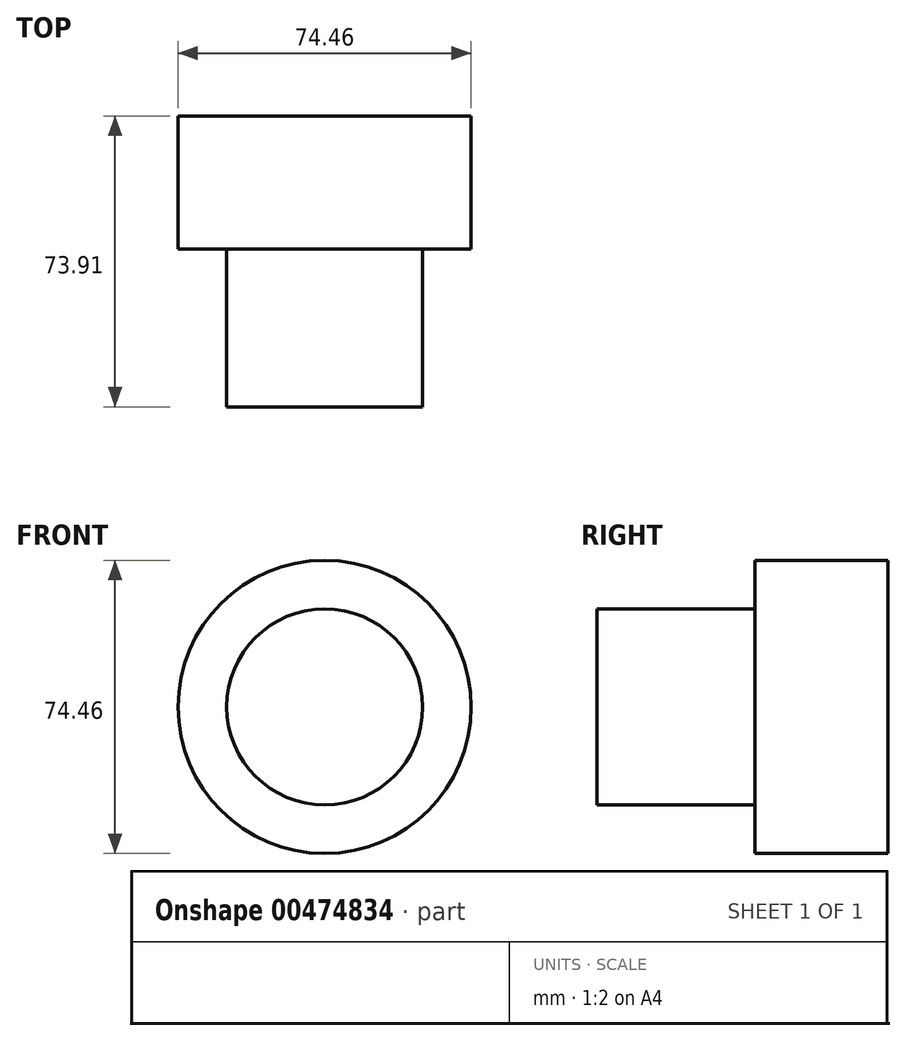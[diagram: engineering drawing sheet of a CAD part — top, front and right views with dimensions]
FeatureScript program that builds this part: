
annotation { "Feature Type Name" : "Feature", "Feature Type Description" : "" }
export const myFeature = defineFeature(function(context is Context, id is Id, definition is map)
    precondition{}
    {
        {
            var Q0;
            Q0=qCreatedBy(makeId("Front.planeOp"),FACE);
            var sketch = newSketch(context, id + "F0", { "sketchPlane" : qUnion([Q0])});
            skCircle(sketch, "E0", {"center": v(0, 0) * mm, "radius": 37.23 * mm});
            skSolve(sketch);
        }
        {
            var Q0;
            Q0=makeQuery(id+"F0.imprint","IMPRINT",FACE,{"disambiguationData":[TD([[makeQuery(id+"F0.imprint","IMPRINT",EDGE,{"derivedFrom":sQuery(id+"F0.wireOp",EDGE,"E0")}),1.0]])]});
            extrude(context, id + "F1", {"entities" : qUnion([Q0]), "oppositeDirection" : true, "depth" : 33.78 * mm});
        }
        {
            var Q0;
            Q0=qCreatedBy(makeId("Front.planeOp"),FACE);
            var sketch = newSketch(context, id + "F2", { "sketchPlane" : qUnion([Q0])});
            skCircle(sketch, "E1", {"center": v(0, 0) * mm, "radius": 24.9 * mm});
            skSolve(sketch);
        }
        {
            var Q0;
            Q0=makeQuery(id+"F2.imprint","IMPRINT",FACE,{"disambiguationData":[TD([[makeQuery(id+"F2.imprint","IMPRINT",EDGE,{"derivedFrom":sQuery(id+"F2.wireOp",EDGE,"E1")}),1.0]])]});
            extrude(context, id + "F3", {"entities" : qUnion([Q0]), "operationType" : NewBodyOperationType.ADD, "depth" : 40.13 * mm});
        }
    });
